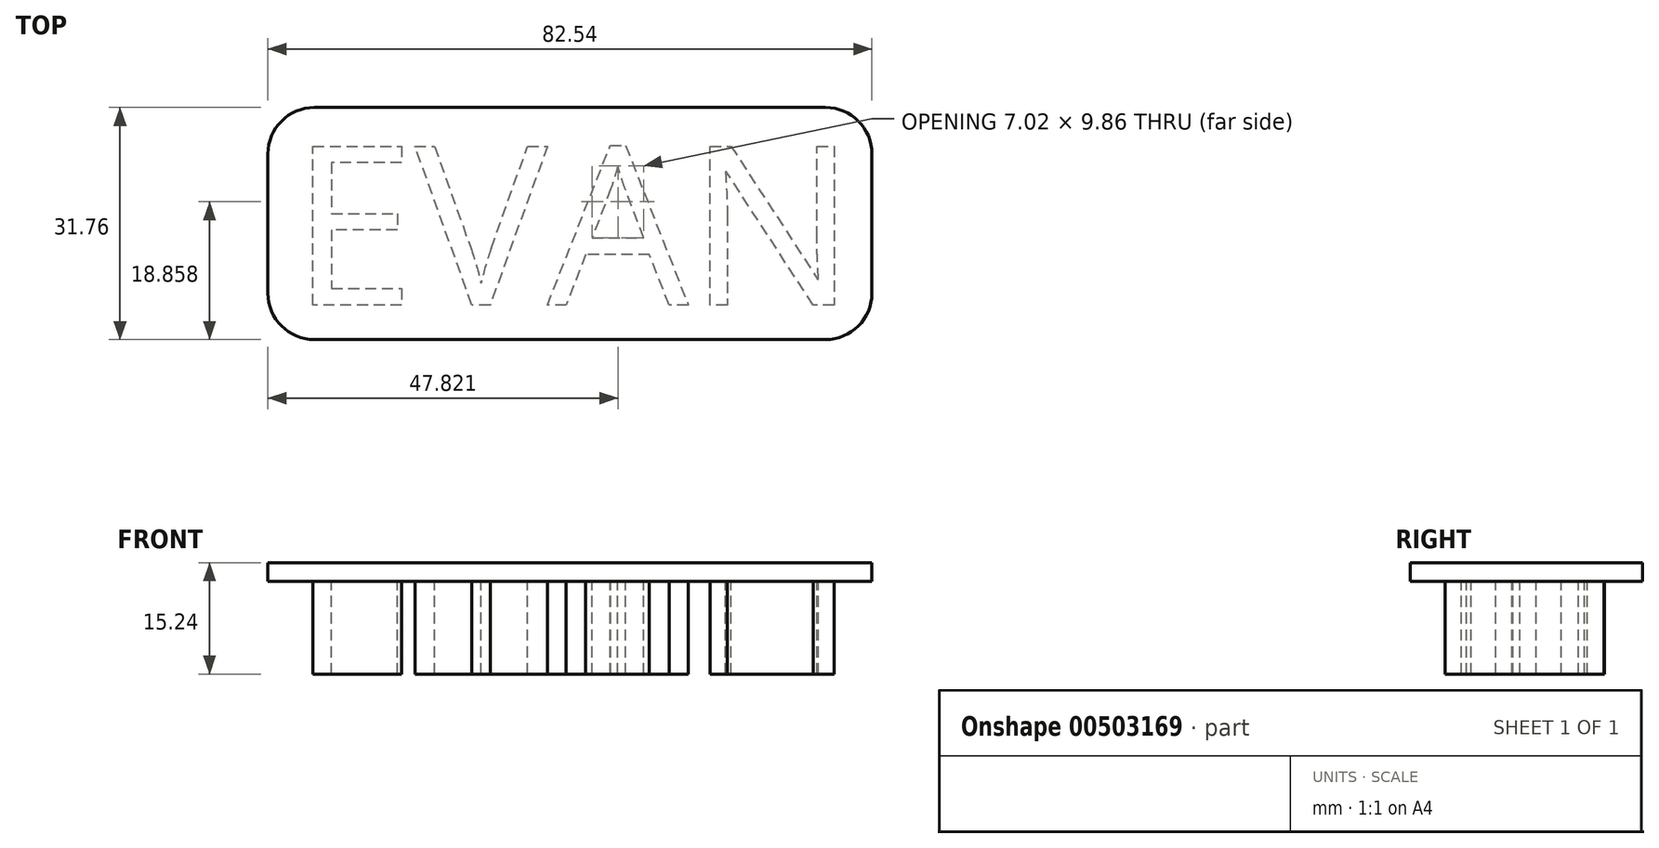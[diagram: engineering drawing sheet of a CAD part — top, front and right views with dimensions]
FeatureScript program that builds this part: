
annotation { "Feature Type Name" : "Feature", "Feature Type Description" : "" }
export const myFeature = defineFeature(function(context is Context, id is Id, definition is map)
    precondition{}
    {
        {
            var Q0;
            Q0=qCreatedBy(makeId("Top.planeOp"),FACE);
            var sketch = newSketch(context, id + "F0", { "sketchPlane" : qUnion([Q0])});
            skText(sketch, "E0", { "text": "EVAN", "fontName": "OpenSans-Regular.ttf"});
            const initialGuessF0  = {"E0": [-0.0381, -0.01113, 1, 0, 0.0219]};
            skSetInitialGuess(sketch, initialGuessF0);
            skSolve(sketch);
        }
        {
            var Q0;
            Q0=qSketchRegion(id+"F0",true);
            extrude(context, id + "F1", {"entities" : qUnion([Q0]), "oppositeDirection" : true, "depth" : 12.7 * mm});
        }
        {
            var Q0;
            Q0=qCreatedBy(makeId("Top.planeOp"),FACE);
            var sketch = newSketch(context, id + "F2", { "sketchPlane" : qUnion([Q0])});
            skLineSegment(sketch, "E1.bottom", {"start": v(41.28, 15.88) * mm, "end": v(-41.28, 15.88) * mm});
            skLineSegment(sketch, "E1.top", {"start": v(41.28, -15.88) * mm, "end": v(-41.28, -15.88) * mm});
            skLineSegment(sketch, "E1.left", {"start": v(41.28, 15.88) * mm, "end": v(41.28, -15.88) * mm});
            skLineSegment(sketch, "E1.right", {"start": v(-41.28, 15.88) * mm, "end": v(-41.28, -15.88) * mm});
            skPoint(sketch, "E1.middle", {"position": v(0, 0) * mm});
            skSolve(sketch);
        }
        {
            var Q0;
            Q0=makeQuery(id+"F2.imprint","IMPRINT",FACE,{"disambiguationData":[TD([[makeQuery(id+"F2.imprint","IMPRINT",EDGE,{"derivedFrom":sQuery(id+"F2.wireOp",EDGE,"E1.bottom")}),1.0]])]});
            extrude(context, id + "F3", {"entities" : qUnion([Q0]), "depth" : 2.54 * mm});
        }
        {
            var Q0;
            Q0=makeQuery(id+"F3.opExtrude","SWEPT_EDGE",EDGE,{"disambiguationData":[OSD([sQuery(id+"F2.wireOp",EDGE,"E1.bottom"),sQuery(id+"F2.wireOp",EDGE,"E1.right")])]});
            var Q1;
            Q1=makeQuery(id+"F3.opExtrude","SWEPT_EDGE",EDGE,{"disambiguationData":[OSD([sQuery(id+"F2.wireOp",EDGE,"E1.top"),sQuery(id+"F2.wireOp",EDGE,"E1.right")])]});
            var Q2;
            Q2=makeQuery(id+"F3.opExtrude","SWEPT_EDGE",EDGE,{"disambiguationData":[OSD([sQuery(id+"F2.wireOp",EDGE,"E1.top"),sQuery(id+"F2.wireOp",EDGE,"E1.left")])]});
            var Q3;
            Q3=makeQuery(id+"F3.opExtrude","SWEPT_EDGE",EDGE,{"disambiguationData":[OSD([sQuery(id+"F2.wireOp",EDGE,"E1.bottom"),sQuery(id+"F2.wireOp",EDGE,"E1.left")])]});
            fillet(context, id + "F4", {"entities" : qUnion([Q0, Q1, Q2, Q3]), "radius" : 6.35 * mm, "tangentPropagation" : true, "allowEdgeOverflow" : false});
        }
    });
